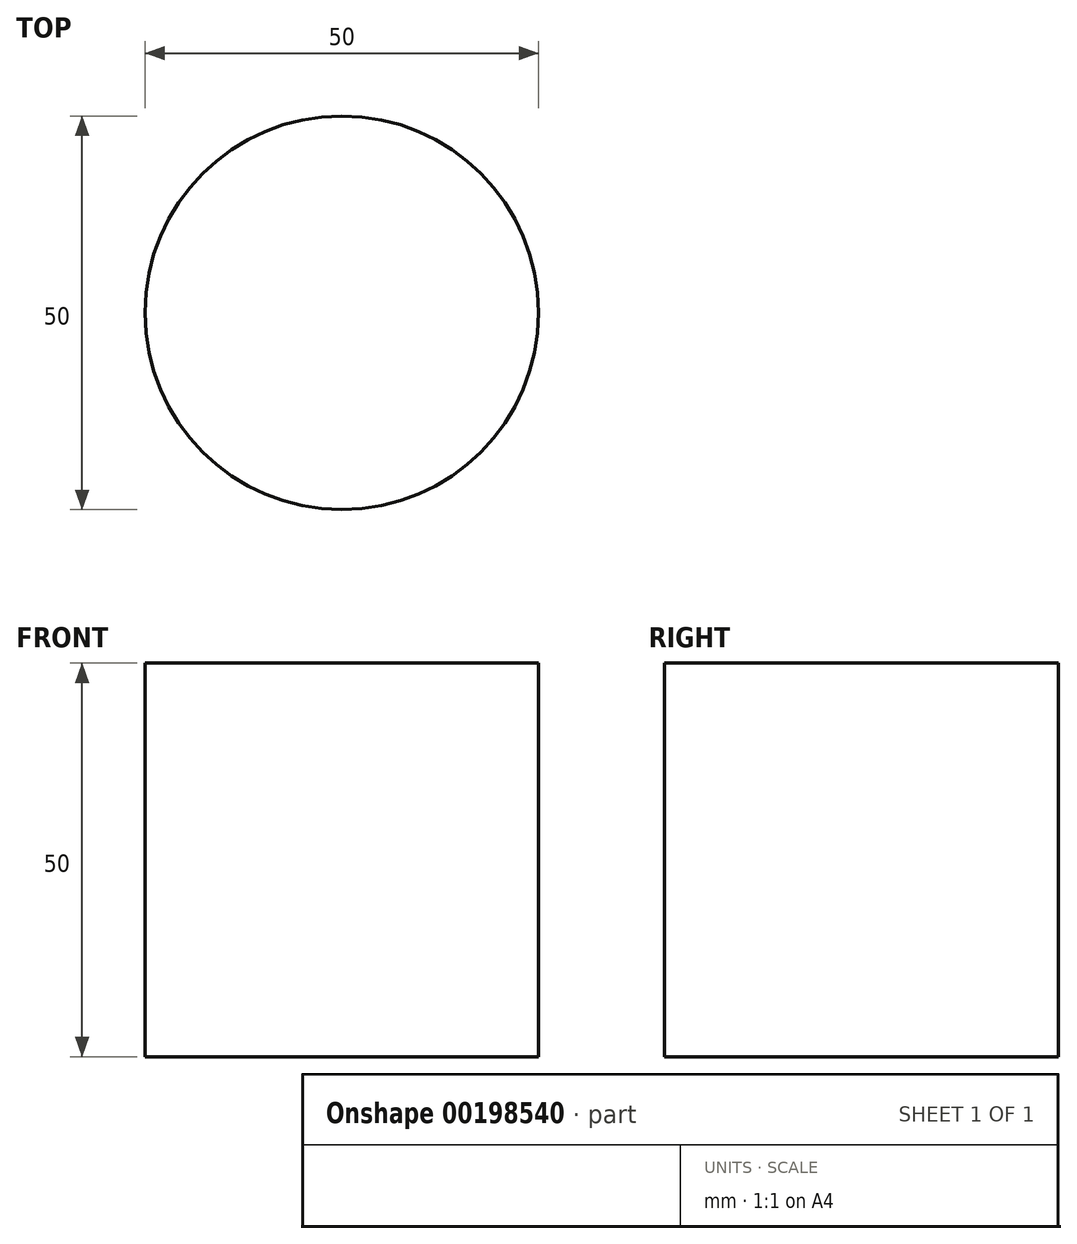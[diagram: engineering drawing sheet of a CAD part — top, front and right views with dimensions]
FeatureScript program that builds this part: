
annotation { "Feature Type Name" : "Feature", "Feature Type Description" : "" }
export const myFeature = defineFeature(function(context is Context, id is Id, definition is map)
    precondition{}
    {
        {
            var Q0;
            Q0=qCreatedBy(makeId("Front.planeOp"),FACE);
            var sketch = newSketch(context, id + "F0", { "sketchPlane" : qUnion([Q0])});
            skLineSegment(sketch, "E0.bottom", {"start": v(0, 0) * mm, "end": v(150, 0) * mm, "construction": true});
            skLineSegment(sketch, "E0.top", {"start": v(0, 50) * mm, "end": v(150, 50) * mm, "construction": true});
            skLineSegment(sketch, "E0.left", {"start": v(0, 0) * mm, "end": v(0, 50) * mm, "construction": true});
            skLineSegment(sketch, "E0.right", {"start": v(150, 0) * mm, "end": v(150, 50) * mm, "construction": true});
            skLineSegment(sketch, "E1.bottom", {"start": v(0, 50) * mm, "end": v(50, 50) * mm, "construction": true});
            skLineSegment(sketch, "E1.top", {"start": v(0, 0) * mm, "end": v(50, 0) * mm, "construction": true});
            skLineSegment(sketch, "E1.left", {"start": v(0, 50) * mm, "end": v(0, 0) * mm, "construction": true});
            skLineSegment(sketch, "E1.right", {"start": v(50, 50) * mm, "end": v(50, 0) * mm, "construction": true});
            skLineSegment(sketch, "E2", {"start": v(25, 50) * mm, "end": v(25, 0) * mm, "construction": true});
            skLineSegment(sketch, "E3.bottom", {"start": v(25, 50) * mm, "end": v(50, 50) * mm});
            skLineSegment(sketch, "E3.top", {"start": v(25, 0) * mm, "end": v(50, 0) * mm});
            skLineSegment(sketch, "E3.left", {"start": v(25, 50) * mm, "end": v(25, 0) * mm});
            skLineSegment(sketch, "E3.right", {"start": v(50, 50) * mm, "end": v(50, 0) * mm});
            skLineSegment(sketch, "E4", {"start": v(50, 25) * mm, "end": v(150, 25) * mm, "construction": true});
            skLineSegment(sketch, "E5", {"start": v(50, 25) * mm, "end": v(50, 0) * mm, "construction": true});
            skLineSegment(sketch, "E6", {"start": v(50, 12.5) * mm, "end": v(150, 12.5) * mm, "construction": true});
            skLineSegment(sketch, "E7", {"start": v(50, 50) * mm, "end": v(50, 25) * mm, "construction": true});
            skLineSegment(sketch, "E8", {"start": v(50, 37.5) * mm, "end": v(150, 37.5) * mm, "construction": true});
            skLineSegment(sketch, "E9", {"start": v(100, 37.5) * mm, "end": v(100, 50) * mm, "construction": true});
            skLineSegment(sketch, "E10", {"start": v(100, 50) * mm, "end": v(100, 0) * mm, "construction": true});
            skLineSegment(sketch, "E11", {"start": v(50, 50) * mm, "end": v(100, 50) * mm, "construction": true});
            skLineSegment(sketch, "E12", {"start": v(75, 50) * mm, "end": v(75, 0) * mm, "construction": true});
            skLineSegment(sketch, "E13", {"start": v(100, 50) * mm, "end": v(150, 50) * mm, "construction": true});
            skLineSegment(sketch, "E14", {"start": v(125, 50) * mm, "end": v(125, 0) * mm, "construction": true});
            skLineSegment(sketch, "E15", {"start": v(75, 37.5) * mm, "end": v(75, 25) * mm, "construction": true});
            skLineSegment(sketch, "E16", {"start": v(50, 37.5) * mm, "end": v(50, 25) * mm, "construction": true});
            skLineSegment(sketch, "E17", {"start": v(50, 31.25) * mm, "end": v(75, 31.25) * mm, "construction": true});
            skLineSegment(sketch, "E18", {"start": v(75, 0) * mm, "end": v(75, 12.5) * mm, "construction": true});
            skLineSegment(sketch, "E19", {"start": v(50, 12.5) * mm, "end": v(50, 0) * mm, "construction": true});
            skLineSegment(sketch, "E20", {"start": v(50, 6.25) * mm, "end": v(75, 5.5) * mm, "construction": true});
            skLineSegment(sketch, "E21", {"start": v(50, 50) * mm, "end": v(50, 37.5) * mm, "construction": true});
            skLineSegment(sketch, "E22", {"start": v(150, 50) * mm, "end": v(150, 37.5) * mm, "construction": true});
            skLineSegment(sketch, "E23", {"start": v(150, 43.75) * mm, "end": v(50, 43.75) * mm, "construction": true});
            skArc(sketch, "E24", {"start": v(75, 25) * mm, "mid": v(111.98, 15.65) * mm, "end": v(150, 12.5) * mm});
            skArc(sketch, "E25", {"start": v(100, 17.97) * mm, "mid": v(73.88, 12.1) * mm, "end": v(50, 0) * mm});
            skArc(sketch, "E26", {"start": v(100, 30.47) * mm, "mid": v(73.88, 24.6) * mm, "end": v(50, 12.5) * mm});
            skArc(sketch, "E27", {"start": v(75, 25) * mm, "mid": v(63.98, 34.2) * mm, "end": v(50, 37.5) * mm});
            skFitSpline(sketch, "E28", {"points": [v(50, 50) * mm, v(100, 30.47) * mm, v(150, 25) * mm], "startDerivative": vector(97.57, -45.37) * mm, "endDerivative": vector(102.45, -4.4) * mm});
            skLineSegment(sketch, "E29", {"start": v(150, 25) * mm, "end": v(150, 12.5) * mm});
            skSolve(sketch);
        }
        {
            var Q0;
            Q0=makeQuery(id+"F0.imprint","IMPRINT",FACE,{"disambiguationData":[TD([[makeQuery(id+"F0.imprint","IMPRINT",EDGE,{"derivedFrom":sQuery(id+"F0.wireOp",EDGE,"E3.bottom")}),-1.0]])]});
            var Q1;
            Q1=sQuery(id+"F0.wireOp",EDGE,"E3.left");
            revolve(context, id + "F1", {"entities" : qUnion([Q0]), "axis" : qUnion([Q1]), "revolveType" : RevolveType.FULL});
        }
    });
